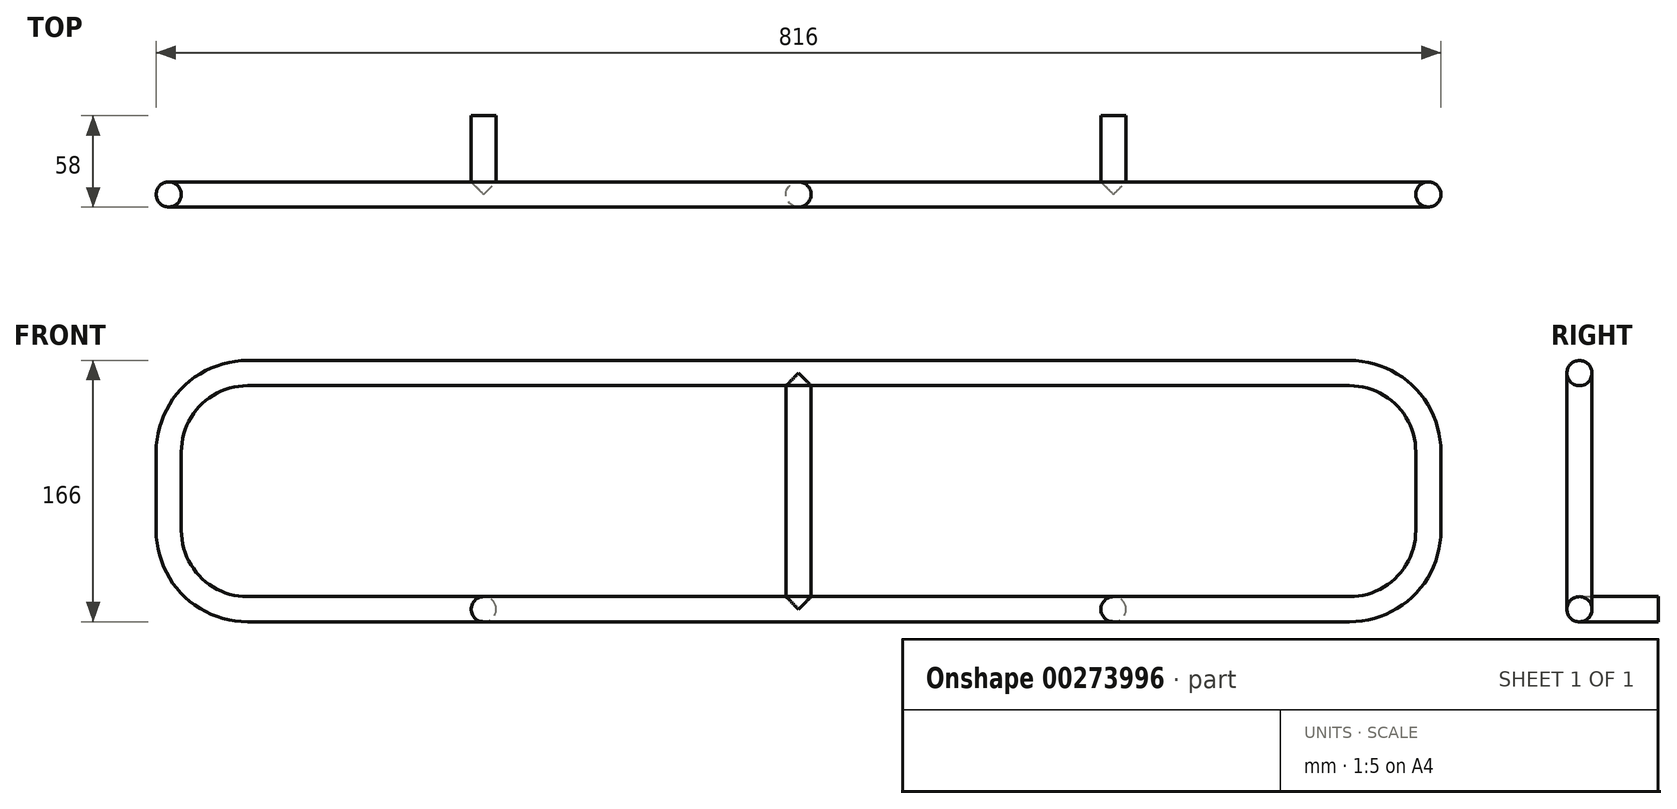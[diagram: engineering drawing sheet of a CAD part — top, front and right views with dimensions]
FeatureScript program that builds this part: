
annotation { "Feature Type Name" : "Feature", "Feature Type Description" : "" }
export const myFeature = defineFeature(function(context is Context, id is Id, definition is map)
    precondition{}
    {
        {
            var Q0;
            Q0=qCreatedBy(makeId("Front.planeOp"),FACE);
            var sketch = newSketch(context, id + "F0", { "sketchPlane" : qUnion([Q0])});
            skLineSegment(sketch, "E0.bottom", {"start": v(-350, 0) * mm, "end": v(350, 0) * mm});
            skLineSegment(sketch, "E0.top", {"start": v(-350, 150) * mm, "end": v(350, 150) * mm});
            skLineSegment(sketch, "E0.left", {"start": v(-400, 50) * mm, "end": v(-400, 100) * mm});
            skLineSegment(sketch, "E0.right", {"start": v(400, 50) * mm, "end": v(400, 100) * mm});
            skPoint(sketch, "E1.visualSharp", {"position": v(-400, 150) * mm});
            skArc(sketch, "E1.filletArc", {"start": v(-350, 150) * mm, "mid": v(-385.36, 135.36) * mm, "end": v(-400, 100) * mm});
            skPoint(sketch, "E2.visualSharp", {"position": v(-400, 0) * mm});
            skArc(sketch, "E2.filletArc", {"start": v(-400, 50) * mm, "mid": v(-385.36, 14.64) * mm, "end": v(-350, 0) * mm});
            skPoint(sketch, "E3.visualSharp", {"position": v(400, 150) * mm});
            skArc(sketch, "E3.filletArc", {"start": v(400, 100) * mm, "mid": v(385.36, 135.36) * mm, "end": v(350, 150) * mm});
            skPoint(sketch, "E4.visualSharp", {"position": v(400, 0) * mm});
            skArc(sketch, "E4.filletArc", {"start": v(350, 0) * mm, "mid": v(385.36, 14.64) * mm, "end": v(400, 50) * mm});
            skSolve(sketch);
        }
        {
            var Q0;
            Q0=qCreatedBy(makeId("Right.planeOp"),FACE);
            var Q1;
            Q1=sQuery(id+"F0.wireOp",VERTEX,"E2.filletArc.end");
            cPlane(context, id + "F1", {"entities" : qUnion([Q0, Q1]), "cplaneType" : CPlaneType.PLANE_POINT, "offset" : 150 * mm, "width" : 150 * mm, "height" : 150 * mm});
        }
        {
            var Q0;
            Q0=qCreatedBy(id+"F1.planeOp",FACE);
            var sketch = newSketch(context, id + "F2", { "sketchPlane" : qUnion([Q0])});
            skCircle(sketch, "E5", {"center": v(0, 0) * mm, "radius": 8 * mm});
            skSolve(sketch);
        }
        {
            var Q0;
            Q0=makeQuery(id+"F2.imprint","IMPRINT",FACE,{"disambiguationData":[TD([[makeQuery(id+"F2.imprint","IMPRINT",EDGE,{"derivedFrom":sQuery(id+"F2.wireOp",EDGE,"E5")}),1.0]])]});
            var Q1;
            Q1=sQuery(id+"F0.wireOp",EDGE,"E0.bottom");
            var Q2;
            Q2=sQuery(id+"F0.wireOp",EDGE,"E4.filletArc");
            var Q3;
            Q3=sQuery(id+"F0.wireOp",EDGE,"E0.right");
            var Q4;
            Q4=sQuery(id+"F0.wireOp",EDGE,"E3.filletArc");
            var Q5;
            Q5=sQuery(id+"F0.wireOp",EDGE,"E0.top");
            var Q6;
            Q6=sQuery(id+"F0.wireOp",EDGE,"E1.filletArc");
            var Q7;
            Q7=sQuery(id+"F0.wireOp",EDGE,"E0.left");
            var Q8;
            Q8=sQuery(id+"F0.wireOp",EDGE,"E2.filletArc");
            sweep(context, id + "F3", {"profiles" : qUnion([Q0]), "path" : qUnion([Q1, Q2, Q3, Q4, Q5, Q6, Q7, Q8])});
        }
        {
            var Q0;
            Q0=qCreatedBy(makeId("Top.planeOp"),FACE);
            cPlane(context, id + "F4", {"entities" : qUnion([Q0]), "cplaneType" : CPlaneType.OFFSET, "offset" : 50 * mm, "width" : 150 * mm, "height" : 150 * mm});
        }
        {
            var Q0;
            Q0=qCreatedBy(id+"F4.planeOp",FACE);
            var sketch = newSketch(context, id + "F5", { "sketchPlane" : qUnion([Q0])});
            skCircle(sketch, "E6", {"center": v(0, 0) * mm, "radius": 8 * mm});
            skSolve(sketch);
        }
        {
            var Q0;
            Q0=qSketchRegion(id+"F5",true);
            var Q1;
            Q1=makeQuery(id+"F3.opSweep","SWEPT_FACE",FACE,{"disambiguationData":[OSD([sQuery(id+"F0.wireOp",EDGE,"E0.top"),sQuery(id+"F2.wireOp",EDGE,"E5")])]});
            var Q2;
            Q2=makeQuery(id+"F3.opSweep","SWEPT_FACE",FACE,{"disambiguationData":[OSD([sQuery(id+"F0.wireOp",EDGE,"E0.bottom"),sQuery(id+"F2.wireOp",EDGE,"E5")])]});
            extrude(context, id + "F6", {"entities" : qUnion([Q0]), "endBound" : BoundingType.UP_TO_SURFACE, "endBoundEntityFace" : qUnion([Q1]), "depth" : 25 * mm, "hasSecondDirection" : true, "secondDirectionBound" : SecondDirectionBoundingType.UP_TO_SURFACE, "secondDirectionOppositeDirection" : true, "secondDirectionBoundEntityFace" : qUnion([Q2]), "secondDirectionDepth" : 25 * mm});
        }
        {
            var Q0;
            Q0=qCreatedBy(makeId("Front.planeOp"),FACE);
            cPlane(context, id + "F7", {"entities" : qUnion([Q0]), "cplaneType" : CPlaneType.OFFSET, "offset" : 50 * mm, "oppositeDirection" : true, "width" : 150 * mm, "height" : 150 * mm});
        }
        {
            var Q0;
            Q0=qCreatedBy(id+"F7.planeOp",FACE);
            var sketch = newSketch(context, id + "F8", { "sketchPlane" : qUnion([Q0])});
            skCircle(sketch, "E7", {"center": v(200, 0) * mm, "radius": 8 * mm});
            skCircle(sketch, "E8", {"center": v(-200, 0) * mm, "radius": 8 * mm});
            skLineSegment(sketch, "E9", {"start": v(0, 0) * mm, "end": v(0, 89) * mm, "construction": true});
            skSolve(sketch);
        }
        {
            var Q0;
            Q0=qSketchRegion(id+"F8",true);
            var Q1;
            Q1=makeQuery(id+"F3.opSweep","SWEPT_FACE",FACE,{"disambiguationData":[OSD([sQuery(id+"F0.wireOp",EDGE,"E0.bottom"),sQuery(id+"F2.wireOp",EDGE,"E5")])]});
            extrude(context, id + "F9", {"entities" : qUnion([Q0]), "endBound" : BoundingType.UP_TO_SURFACE, "endBoundEntityFace" : qUnion([Q1]), "depth" : 25 * mm});
        }
    });
